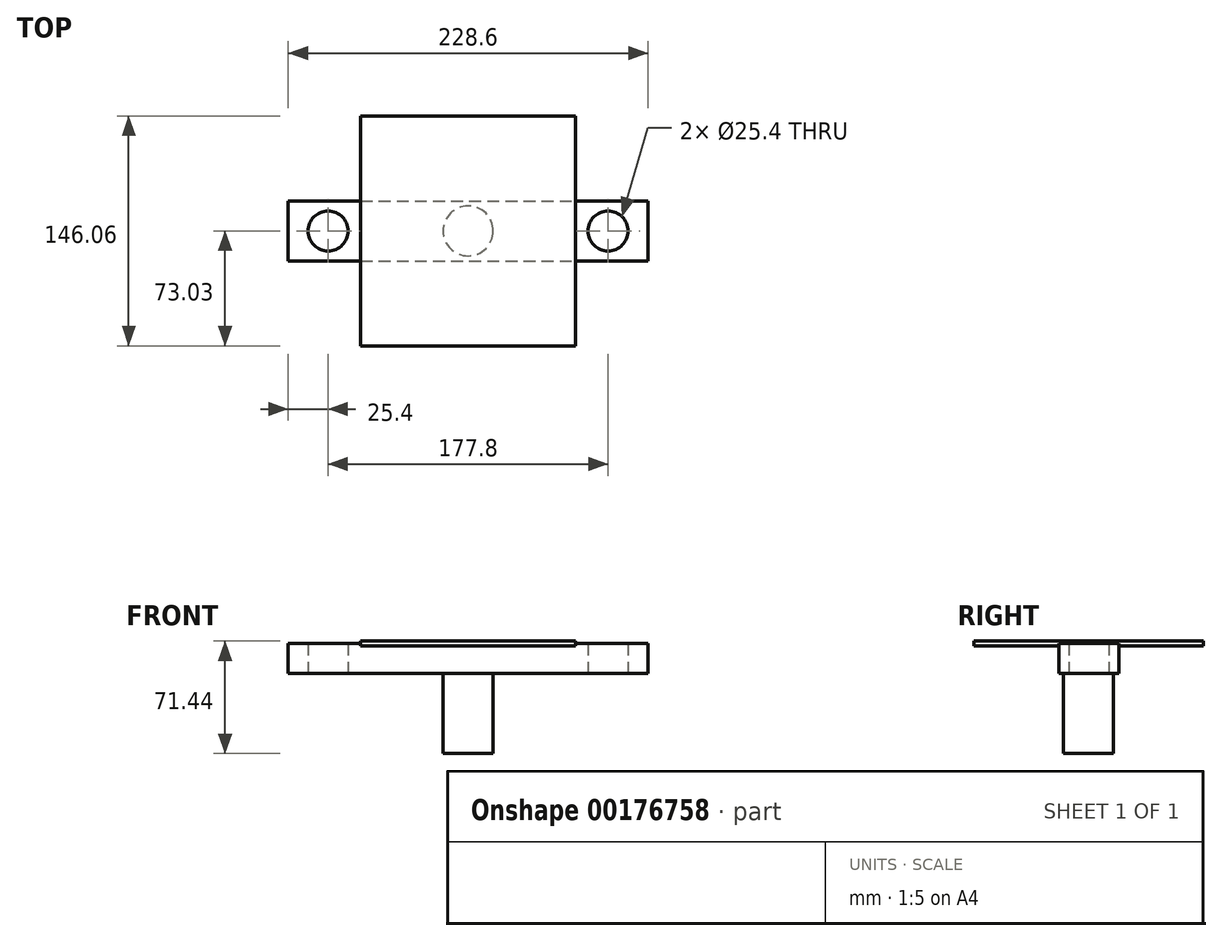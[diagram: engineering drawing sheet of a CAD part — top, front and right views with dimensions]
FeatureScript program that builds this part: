
annotation { "Feature Type Name" : "Feature", "Feature Type Description" : "" }
export const myFeature = defineFeature(function(context is Context, id is Id, definition is map)
    precondition{}
    {
        {
            var Q0;
            Q0=qCreatedBy(makeId("Top.planeOp"),FACE);
            var sketch = newSketch(context, id + "F0", { "sketchPlane" : qUnion([Q0])});
            skLineSegment(sketch, "E0.bottom", {"start": v(-114.3, 19.05) * mm, "end": v(114.3, 19.05) * mm});
            skLineSegment(sketch, "E0.top", {"start": v(-114.3, -19.05) * mm, "end": v(114.3, -19.05) * mm});
            skLineSegment(sketch, "E0.left", {"start": v(-114.3, 19.05) * mm, "end": v(-114.3, -19.05) * mm});
            skLineSegment(sketch, "E0.right", {"start": v(114.3, 19.05) * mm, "end": v(114.3, -19.05) * mm});
            skPoint(sketch, "E0.middle", {"position": v(0, 0) * mm});
            skCircle(sketch, "E1", {"center": v(-88.9, 0) * mm, "radius": 12.7 * mm});
            skCircle(sketch, "E2.MirrorC", {"center": v(88.9, 0) * mm, "radius": 12.7 * mm});
            skSolve(sketch);
        }
        {
            var Q0;
            Q0=makeQuery(id+"F0.imprint","IMPRINT",FACE,{"disambiguationData":[TD([[makeQuery(id+"F0.imprint","IMPRINT",EDGE,{"derivedFrom":sQuery(id+"F0.wireOp",EDGE,"E0.bottom")}),-1.0]])]});
            extrude(context, id + "F1", {"entities" : qUnion([Q0]), "depth" : 19.05 * mm});
        }
        {
            var Q0;
            Q0=makeQuery(id+"F1.opExtrude","CAP_FACE",FACE,{"disambiguationData":[OSD([sQuery(id+"F0.wireOp",EDGE,"E0.bottom"),sQuery(id+"F0.wireOp",EDGE,"E0.top"),sQuery(id+"F0.wireOp",EDGE,"E0.left"),sQuery(id+"F0.wireOp",EDGE,"E0.right"),sQuery(id+"F0.wireOp",EDGE,"E1"),sQuery(id+"F0.wireOp",EDGE,"E2.MirrorC")])],"isStart":false});
            var sketch = newSketch(context, id + "F2", { "sketchPlane" : qUnion([Q0])});
            skLineSegment(sketch, "E3.bottom", {"start": v(-68.26, 73.03) * mm, "end": v(68.26, 73.03) * mm});
            skLineSegment(sketch, "E3.top", {"start": v(-68.26, -73.03) * mm, "end": v(68.26, -73.03) * mm});
            skLineSegment(sketch, "E3.left", {"start": v(-68.26, 73.03) * mm, "end": v(-68.26, -73.03) * mm});
            skLineSegment(sketch, "E3.right", {"start": v(68.26, 73.03) * mm, "end": v(68.26, -73.03) * mm});
            skPoint(sketch, "E3.middle", {"position": v(0, 0) * mm});
            skSolve(sketch);
        }
        {
            var Q0;
            {var subQ0=sQuery(id+"F2.wireOp",EDGE,"E3.left");var subQ1=makeQuery(id+"F1.opExtrude","CAP_EDGE",EDGE,{"disambiguationData":[OSD([sQuery(id+"F0.wireOp",EDGE,"E0.bottom")])],"isStart":false});var subQ2=makeQuery(id+"F2.imprint","INTERSECT",VERTEX,{"derivedFrom":[subQ1,subQ0]});Q0=makeQuery(id+"F2.imprint","IMPRINT",FACE,{"disambiguationData":[TD([[makeQuery(id+"F2.imprint","IMPRINT",EDGE,{"disambiguationData":[TD([[subQ2,-1.0]])],"derivedFrom":subQ0}),1.0]])]});}
            var Q1;
            {var subQ0=sQuery(id+"F2.wireOp",EDGE,"E3.bottom");Q1=makeQuery(id+"F2.imprint","IMPRINT",FACE,{"disambiguationData":[TD([[makeQuery(id+"F2.imprint","IMPRINT",EDGE,{"derivedFrom":subQ0}),-1.0]])]});}
            var Q2;
            {var subQ0=sQuery(id+"F2.wireOp",EDGE,"E3.top");Q2=makeQuery(id+"F2.imprint","IMPRINT",FACE,{"disambiguationData":[TD([[makeQuery(id+"F2.imprint","IMPRINT",EDGE,{"derivedFrom":subQ0}),1.0]])]});}
            extrude(context, id + "F3", {"entities" : qUnion([Q0, Q1, Q2]), "operationType" : NewBodyOperationType.ADD, "endBound" : BoundingType.SYMMETRIC, "depth" : 3.17 * mm});
        }
        {
            var Q0;
            Q0=makeQuery(id+"F1.opExtrude","CAP_FACE",FACE,{"disambiguationData":[OSD([sQuery(id+"F0.wireOp",EDGE,"E0.bottom"),sQuery(id+"F0.wireOp",EDGE,"E0.top"),sQuery(id+"F0.wireOp",EDGE,"E0.left"),sQuery(id+"F0.wireOp",EDGE,"E0.right"),sQuery(id+"F0.wireOp",EDGE,"E1"),sQuery(id+"F0.wireOp",EDGE,"E2.MirrorC")])],"isStart":true});
            var sketch = newSketch(context, id + "F4", { "sketchPlane" : qUnion([Q0])});
            skCircle(sketch, "E4", {"center": v(0, 0) * mm, "radius": 15.88 * mm});
            skSolve(sketch);
        }
        {
            var Q0;
            Q0=makeQuery(id+"F4.imprint","IMPRINT",FACE,{"disambiguationData":[TD([[makeQuery(id+"F4.imprint","IMPRINT",EDGE,{"derivedFrom":sQuery(id+"F4.wireOp",EDGE,"E4")}),1.0]])]});
            extrude(context, id + "F5", {"entities" : qUnion([Q0]), "operationType" : NewBodyOperationType.ADD, "depth" : 50.8 * mm});
        }
    });
